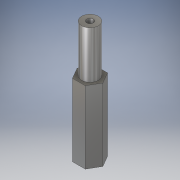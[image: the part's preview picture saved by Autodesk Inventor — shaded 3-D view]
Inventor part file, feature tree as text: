
AUTODESK INVENTOR PART (.ipt)
format: ipt  version: 2017 SP1 (Build 210196100, 196)  size: 110,592 bytes
history: native  units: in
note: dims shown in document units (in); Inventor stores cm internally (conversion verified against a paired STEP export)
features: extrude x2, sketch x2
ambient origin geometry x8: Origin, YZ Plane, XZ Plane, XY Plane, X Axis, Y Axis, Z Axis, Center Point
bodies: Solid1 (feature_tree)
feature tree (4):
  extrude  "Extrusion1"  Depth=1.625in TaperAngle=0.0deg
  extrude  "Extrusion2"  Depth=1.0625in TaperAngle=0.0deg
  sketch  "Sketch1"  dims[d0=0.5in d1=1.625in d2=0.0in]
  sketch  "Sketch2"  dims[d3=0.375in d4=1.0625in d5=0.0in d6=0.15in]
